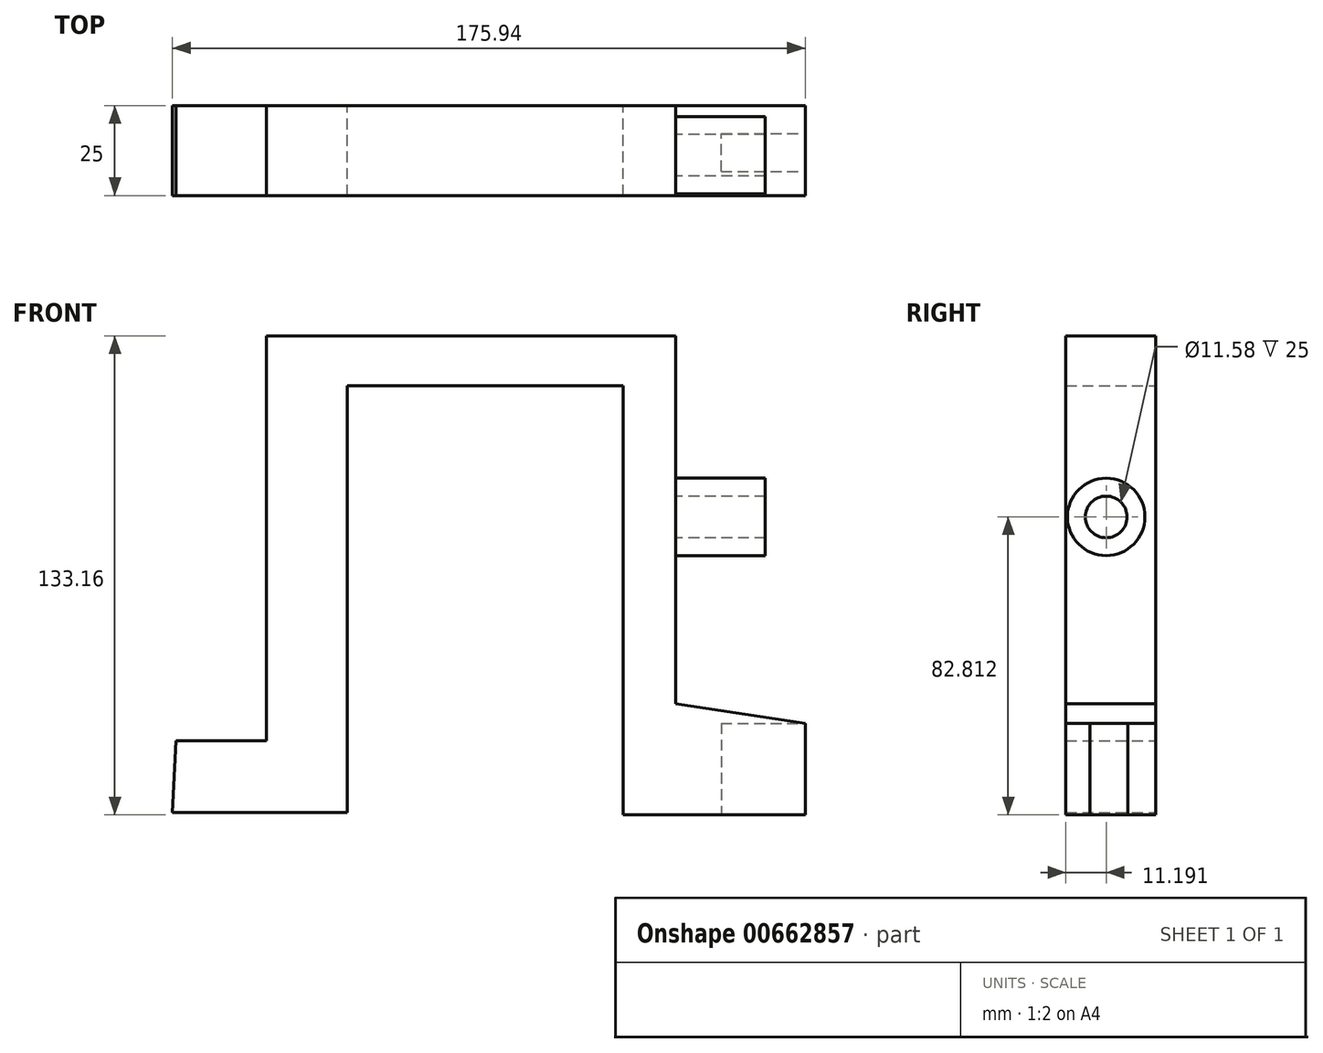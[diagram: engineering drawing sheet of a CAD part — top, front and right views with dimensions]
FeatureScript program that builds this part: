
annotation { "Feature Type Name" : "Feature", "Feature Type Description" : "" }
export const myFeature = defineFeature(function(context is Context, id is Id, definition is map)
    precondition{}
    {
        {
            var Q0;
            Q0=qCreatedBy(makeId("Front.planeOp"),FACE);
            var sketch = newSketch(context, id + "F0", { "sketchPlane" : qUnion([Q0])});
            skLineSegment(sketch, "E0", {"start": v(-101.85, -50.5) * mm, "end": v(-76.67, -50.5) * mm});
            skLineSegment(sketch, "E1", {"start": v(-76.67, -50.5) * mm, "end": v(-76.67, 62.03) * mm});
            skLineSegment(sketch, "E2", {"start": v(-76.67, 62.03) * mm, "end": v(37.08, 62.03) * mm});
            skLineSegment(sketch, "E3", {"start": v(37.08, 62.03) * mm, "end": v(37.08, -40.2) * mm});
            skLineSegment(sketch, "E4", {"start": v(37.08, -40.2) * mm, "end": v(73.18, -45.65) * mm});
            skLineSegment(sketch, "E5", {"start": v(73.18, -45.65) * mm, "end": v(73.18, -71.13) * mm});
            skLineSegment(sketch, "E6", {"start": v(73.18, -71.13) * mm, "end": v(22.52, -71.13) * mm});
            skLineSegment(sketch, "E7", {"start": v(22.52, -71.13) * mm, "end": v(22.52, 48.08) * mm});
            skLineSegment(sketch, "E8", {"start": v(22.52, 48.08) * mm, "end": v(-54.22, 48.08) * mm});
            skLineSegment(sketch, "E9", {"start": v(-54.22, 48.08) * mm, "end": v(-54.22, -70.53) * mm});
            skLineSegment(sketch, "E10", {"start": v(-54.22, -70.53) * mm, "end": v(-102.76, -70.53) * mm});
            skLineSegment(sketch, "E11", {"start": v(-102.76, -70.53) * mm, "end": v(-101.85, -50.5) * mm});
            skSolve(sketch);
        }
        {
            var Q0;
            Q0=makeQuery(id+"F0.imprint","IMPRINT",FACE,{"disambiguationData":[TD([[makeQuery(id+"F0.imprint","IMPRINT",EDGE,{"derivedFrom":sQuery(id+"F0.wireOp",EDGE,"E0")}),-1.0]])]});
            extrude(context, id + "F1", {"entities" : qUnion([Q0]), "depth" : 25 * mm, "offsetDistance" : 25 * mm});
        }
        {
            var Q0;
            Q0=makeQuery(id+"F1.opExtrude","SWEPT_FACE",FACE,{"disambiguationData":[OSD([sQuery(id+"F0.wireOp",EDGE,"E5")])]});
            var sketch = newSketch(context, id + "F2", { "sketchPlane" : qUnion([Q0])});
            skLineSegment(sketch, "E12", {"start": v(-18.33, -45.65) * mm, "end": v(-18.33, -71.13) * mm});
            skLineSegment(sketch, "E13", {"start": v(-18.33, -71.13) * mm, "end": v(-7.75, -71.13) * mm});
            skLineSegment(sketch, "E14", {"start": v(-7.75, -71.13) * mm, "end": v(-7.75, -45.65) * mm});
            skLineSegment(sketch, "E15", {"start": v(-7.75, -45.65) * mm, "end": v(-18.33, -45.65) * mm});
            skSolve(sketch);
        }
        {
            var Q0;
            Q0 = qSketchRegion(id + "F2", true);
            extrude(context, id + "F3", {"entities" : qUnion([Q0]), "operationType" : NewBodyOperationType.REMOVE, "oppositeDirection" : true, "depth" : 23.4 * mm, "offsetDistance" : 25 * mm});
        }
        {
            var Q0;
            Q0=makeQuery(id+"F1.opExtrude","SWEPT_FACE",FACE,{"disambiguationData":[OSD([sQuery(id+"F0.wireOp",EDGE,"E3")])]});
            var sketch = newSketch(context, id + "F4", { "sketchPlane" : qUnion([Q0])});
            skCircle(sketch, "E16", {"center": v(-13.8, 11.68) * mm, "radius": 10.77 * mm});
            skCircle(sketch, "E17", {"center": v(-13.8, 11.68) * mm, "radius": 5.79 * mm});
            skSolve(sketch);
        }
        {
            var Q0;
            Q0 = qSketchRegion(id + "F4", true);
            extrude(context, id + "F5", {"entities" : qUnion([Q0]), "operationType" : NewBodyOperationType.ADD, "depth" : 25 * mm, "offsetDistance" : 25 * mm});
        }
    });
